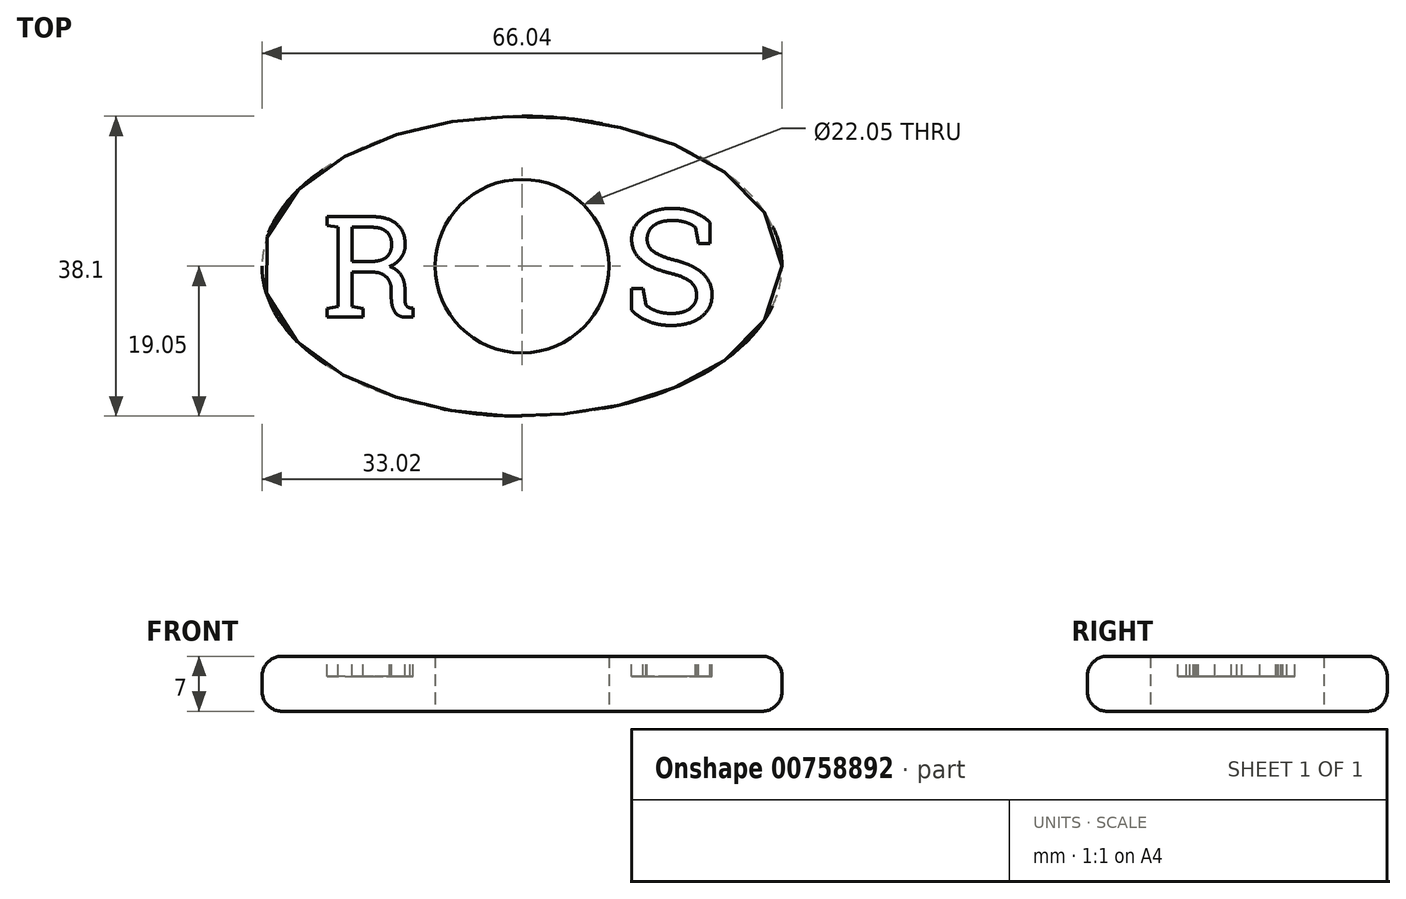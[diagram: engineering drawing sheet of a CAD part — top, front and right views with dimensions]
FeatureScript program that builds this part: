
annotation { "Feature Type Name" : "Feature", "Feature Type Description" : "" }
export const myFeature = defineFeature(function(context is Context, id is Id, definition is map)
    precondition{}
    {
        {
            var Q0;
            Q0=qCreatedBy(makeId("Top.planeOp"),FACE);
            var sketch = newSketch(context, id + "F0", { "sketchPlane" : qUnion([Q0])});
            skEllipse(sketch, "E0", {"center": v(0, 0) * mm, "majorRadius": 33.02 * mm, "minorRadius": 19.05 * mm, "majorAxis": v(1, 0)});
            skCircle(sketch, "E1", {"center": v(0, 0) * mm, "radius": 11.03 * mm});
            skLineSegment(sketch, "E2", {"start": v(-33.02, 0) * mm, "end": v(33.02, 0) * mm, "construction": true});
            skLineSegment(sketch, "E3", {"start": v(0, 19.05) * mm, "end": v(0, -19.05) * mm, "construction": true});
            skSolve(sketch);
        }
        {
            var Q0;
            Q0=makeQuery(id+"F0.imprint","IMPRINT",FACE,{"disambiguationData":[TD([[makeQuery(id+"F0.imprint","IMPRINT",EDGE,{"derivedFrom":sQuery(id+"F0.wireOp",EDGE,"E0")}),1.0]])]});
            extrude(context, id + "F1", {"entities" : qUnion([Q0]), "depth" : 7 * mm, "offsetDistance" : 25.4 * mm});
        }
        {
            var Q0;
            Q0=makeQuery(id+"F1.opExtrude","CAP_EDGE",EDGE,{"disambiguationData":[OSD([sQuery(id+"F0.wireOp",EDGE,"E0")])],"isStart":false});
            var Q1;
            Q1=makeQuery(id+"F1.opExtrude","CAP_EDGE",EDGE,{"disambiguationData":[OSD([sQuery(id+"F0.wireOp",EDGE,"E0")])],"isStart":true});
            fillet(context, id + "F2", {"entities" : qUnion([Q0, Q1]), "radius" : 2.54 * mm, "tangentPropagation" : true, "allowEdgeOverflow" : false});
        }
        {
            var Q0;
            Q0=makeQuery(id+"F1.opExtrude","CAP_FACE",FACE,{"disambiguationData":[OSD([sQuery(id+"F0.wireOp",EDGE,"E0"),sQuery(id+"F0.wireOp",EDGE,"E1")])],"isStart":false});
            var sketch = newSketch(context, id + "F3", { "sketchPlane" : qUnion([Q0])});
            skSolve(sketch);
        }
        {
            var Q0;
            {var subQ0=sQuery(id+"F0.wireOp",EDGE,"E1");Q0=makeQuery(id+"F3.imprint","IMPRINT",FACE,{"disambiguationData":[TD([[makeQuery(id+"F3.imprint","IMPRINT",EDGE,{"derivedFrom":makeQuery(id+"F1.opExtrude","CAP_EDGE",EDGE,{"disambiguationData":[OSD([subQ0])],"isStart":false})}),-1.0]])]});}
            var sketch = newSketch(context, id + "F4", { "sketchPlane" : qUnion([Q0])});
            skText(sketch, "E4", { "text": "R", "fontName": "RobotoSlab-Regular.ttf"});
            skText(sketch, "E5", { "text": "S", "fontName": "RobotoSlab-Regular.ttf"});
            skLineSegment(sketch, "E6", {"start": v(0, 0) * mm, "end": v(-25.4, 0) * mm, "construction": true});
            skLineSegment(sketch, "E7", {"start": v(0, 0) * mm, "end": v(25.4, 0) * mm, "construction": true});
            skLineSegment(sketch, "E8", {"start": v(-25.4, 0) * mm, "end": v(-12.7, 0) * mm, "construction": true});
            skLineSegment(sketch, "E9", {"start": v(12.7, 0) * mm, "end": v(25.4, 0) * mm});
            skPoint(sketch, "E10", {"position": v(19.05, 0) * mm});
            skLineSegment(sketch, "E11", {"start": v(12.7, 0) * mm, "end": v(25.4, 0) * mm, "construction": true});
            skPoint(sketch, "E12", {"position": v(-19.05, 0) * mm});
            const initialGuessF4  = {"E4": [-0.0254, -0.00648, 1, 0, 0.01295], "E5": [0.0127, -0.00733, 1, 0, 0.01465]};
            skSetInitialGuess(sketch, initialGuessF4);
            skSolve(sketch);
        }
        {
            var Q0;
            Q0=qSketchRegion(id+"F4",true);
            extrude(context, id + "F5", {"entities" : qUnion([Q0]), "operationType" : NewBodyOperationType.REMOVE, "oppositeDirection" : true, "depth" : 2.54 * mm, "offsetDistance" : 25.4 * mm});
        }
    });
